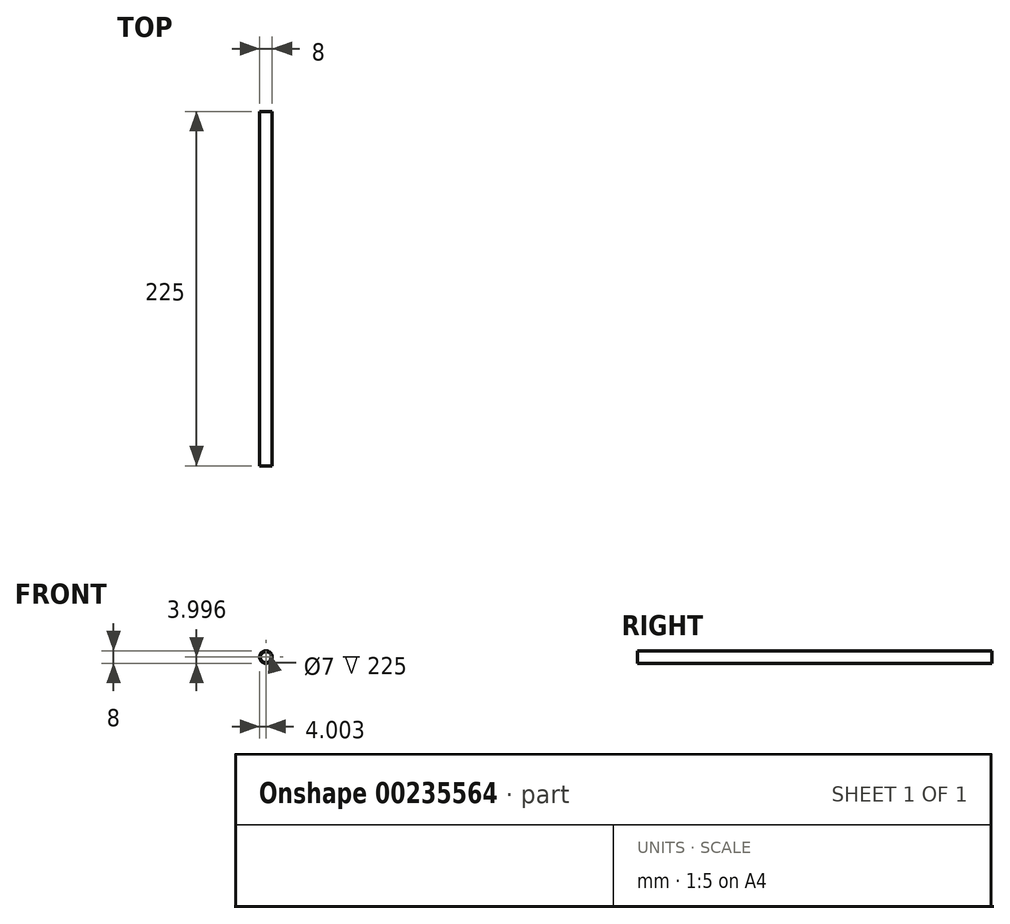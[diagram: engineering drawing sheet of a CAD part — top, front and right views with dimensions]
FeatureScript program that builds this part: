
annotation { "Feature Type Name" : "Feature", "Feature Type Description" : "" }
export const myFeature = defineFeature(function(context is Context, id is Id, definition is map)
    precondition{}
    {
        {
            var Q0;
            Q0=qCreatedBy(makeId("Front.planeOp"),FACE);
            var sketch = newSketch(context, id + "F0", { "sketchPlane" : qUnion([Q0])});
            skCircle(sketch, "E0", {"center": v(-55.57, 33.1) * mm, "radius": 4 * mm});
            skCircle(sketch, "E1", {"center": v(-55.57, 33.1) * mm, "radius": 3.5 * mm});
            skSolve(sketch);
        }
        {
            var Q0;
            Q0 = qSketchRegion(id + "F0", true);
            extrude(context, id + "F1", {"entities" : qUnion([Q0]), "depth" : 225 * mm});
        }
    });
